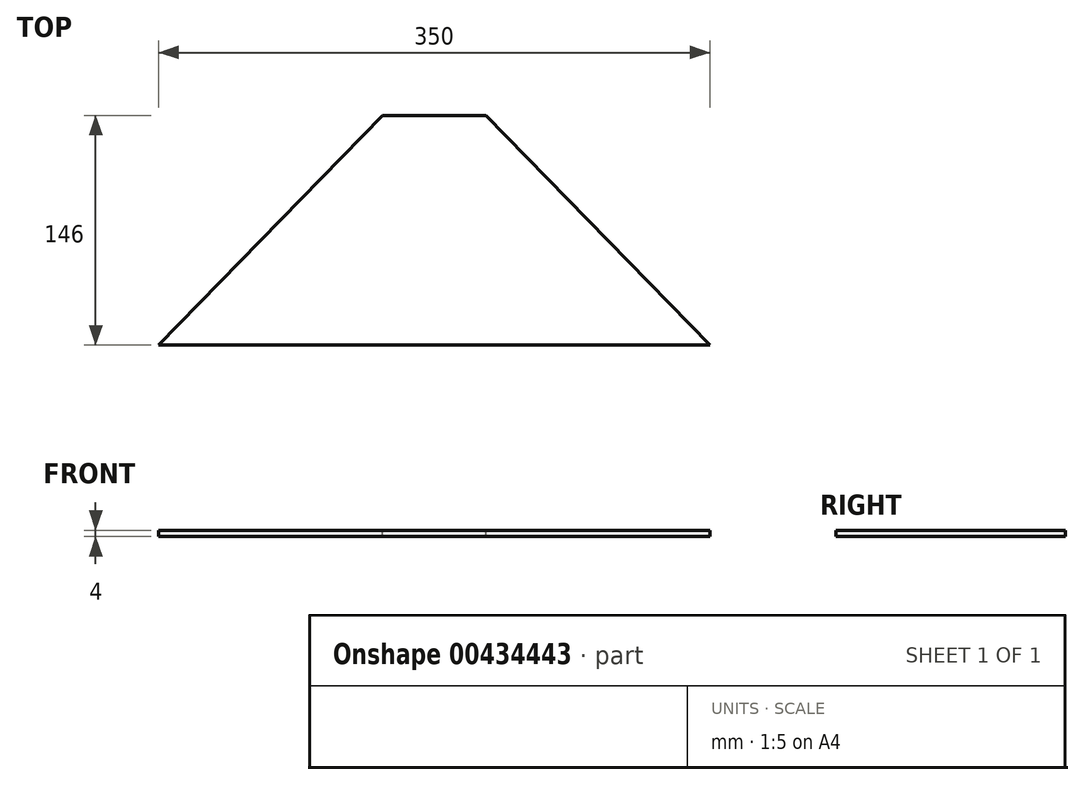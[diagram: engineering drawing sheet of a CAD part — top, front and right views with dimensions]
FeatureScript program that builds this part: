
annotation { "Feature Type Name" : "Feature", "Feature Type Description" : "" }
export const myFeature = defineFeature(function(context is Context, id is Id, definition is map)
    precondition{}
    {
        {
            var Q0;
            Q0=qCreatedBy(makeId("Right.planeOp"),FACE);
            var sketch = newSketch(context, id + "F0", { "sketchPlane" : qUnion([Q0])});
            skLineSegment(sketch, "E0.bottom", {"start": v(-146, 4) * mm, "end": v(0, 4) * mm});
            skLineSegment(sketch, "E1.top", {"start": v(-146, 0) * mm, "end": v(0, 0) * mm});
            skLineSegment(sketch, "E2.trimOffspring", {"start": v(-146, 0) * mm, "end": v(-146, 4) * mm});
            skLineSegment(sketch, "E3", {"start": v(0, 0) * mm, "end": v(0, 4) * mm});
            skSolve(sketch);
        }
        {
            var Q0;
            Q0=qSketchRegion(id+"F0",true);
            extrude(context, id + "F1", {"entities" : qUnion([Q0]), "endBound" : BoundingType.SYMMETRIC, "depth" : 350 * mm, "offsetDistance" : 25 * mm});
        }
        {
            var Q0;
            Q0=makeQuery(id+"F1.opExtrude","SWEPT_FACE",FACE,{"disambiguationData":[OSD([sQuery(id+"F0.wireOp",EDGE,"E0.bottom")])]});
            var sketch = newSketch(context, id + "F2", { "sketchPlane" : qUnion([Q0])});
            skLineSegment(sketch, "E4", {"start": v(-175, -146) * mm, "end": v(-33, 0) * mm});
            skLineSegment(sketch, "E5", {"start": v(-33, 0) * mm, "end": v(-175, 0) * mm});
            skLineSegment(sketch, "E6", {"start": v(-175, 0) * mm, "end": v(-175, -146) * mm});
            skLineSegment(sketch, "E7", {"start": v(175, -146) * mm, "end": v(33, 0) * mm});
            skLineSegment(sketch, "E8", {"start": v(33, 0) * mm, "end": v(175, 0) * mm});
            skLineSegment(sketch, "E9", {"start": v(175, 0) * mm, "end": v(175, -146) * mm});
            skLineSegment(sketch, "E10", {"start": v(0, -146) * mm, "end": v(0, 0) * mm, "construction": true});
            skSolve(sketch);
        }
        {
            var Q0;
            Q0 = qSketchRegion(id + "F2", true);
            extrude(context, id + "F3", {"entities" : qUnion([Q0]), "operationType" : NewBodyOperationType.REMOVE, "endBound" : BoundingType.UP_TO_NEXT, "oppositeDirection" : true, "depth" : 25 * mm, "offsetDistance" : 25 * mm});
        }
    });
